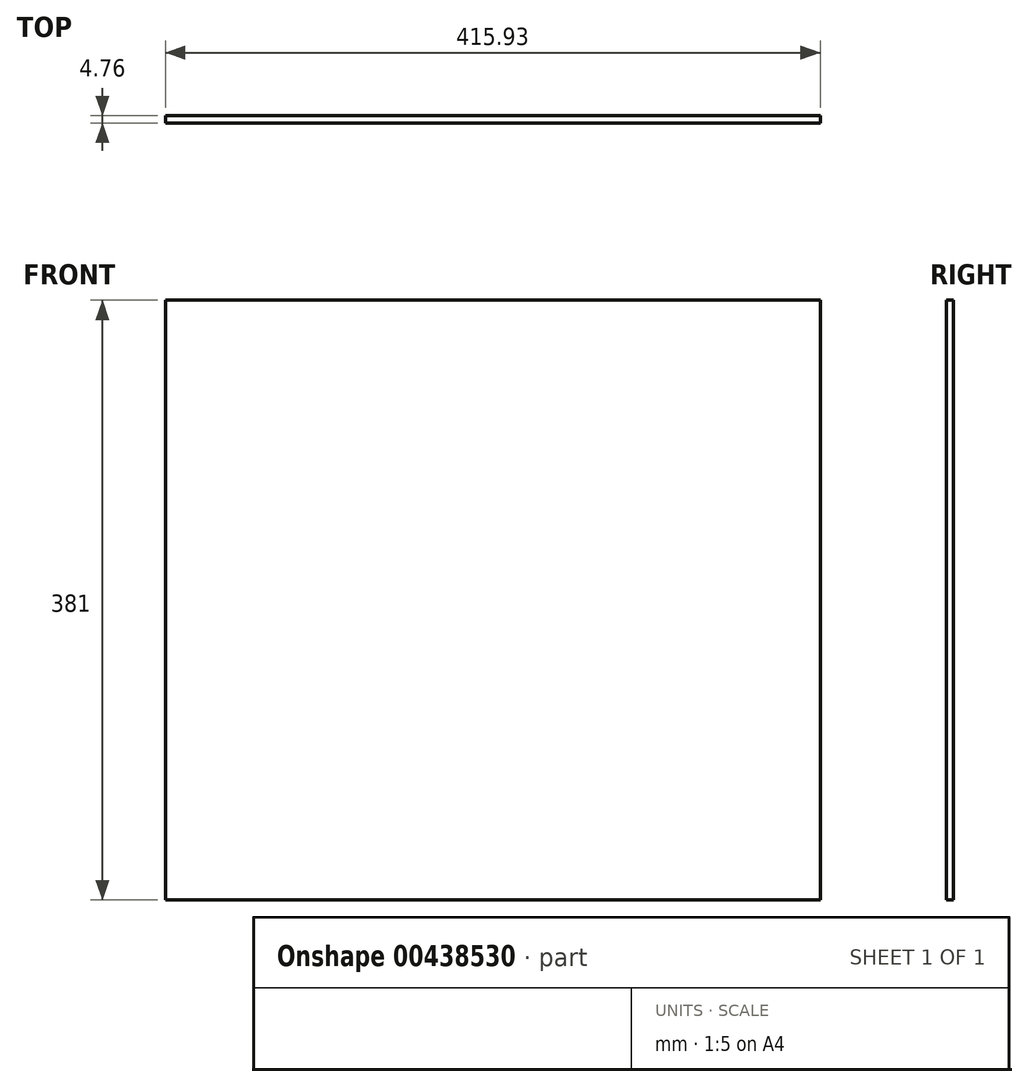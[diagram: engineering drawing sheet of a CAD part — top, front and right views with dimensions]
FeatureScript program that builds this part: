
annotation { "Feature Type Name" : "Feature", "Feature Type Description" : "" }
export const myFeature = defineFeature(function(context is Context, id is Id, definition is map)
    precondition{}
    {
        {
            var Q0;
            Q0=qCreatedBy(makeId("Front.planeOp"),FACE);
            var sketch = newSketch(context, id + "F0", { "sketchPlane" : qUnion([Q0])});
            skLineSegment(sketch, "E0.bottom", {"start": v(-218.07, 276.14) * mm, "end": v(197.86, 276.14) * mm});
            skLineSegment(sketch, "E0.top", {"start": v(-218.07, -104.86) * mm, "end": v(197.86, -104.86) * mm});
            skLineSegment(sketch, "E0.left", {"start": v(-218.07, 276.14) * mm, "end": v(-218.07, -104.86) * mm});
            skLineSegment(sketch, "E0.right", {"start": v(197.86, 276.14) * mm, "end": v(197.86, -104.86) * mm});
            skSolve(sketch);
        }
        {
            var Q0;
            Q0=makeQuery(id+"F0.imprint","IMPRINT",FACE,{"disambiguationData":[TD([[makeQuery(id+"F0.imprint","IMPRINT",EDGE,{"derivedFrom":sQuery(id+"F0.wireOp",EDGE,"E0.bottom")}),-1.0]])]});
            extrude(context, id + "F1", {"entities" : qUnion([Q0]), "depth" : 4.76 * mm});
        }
    });
